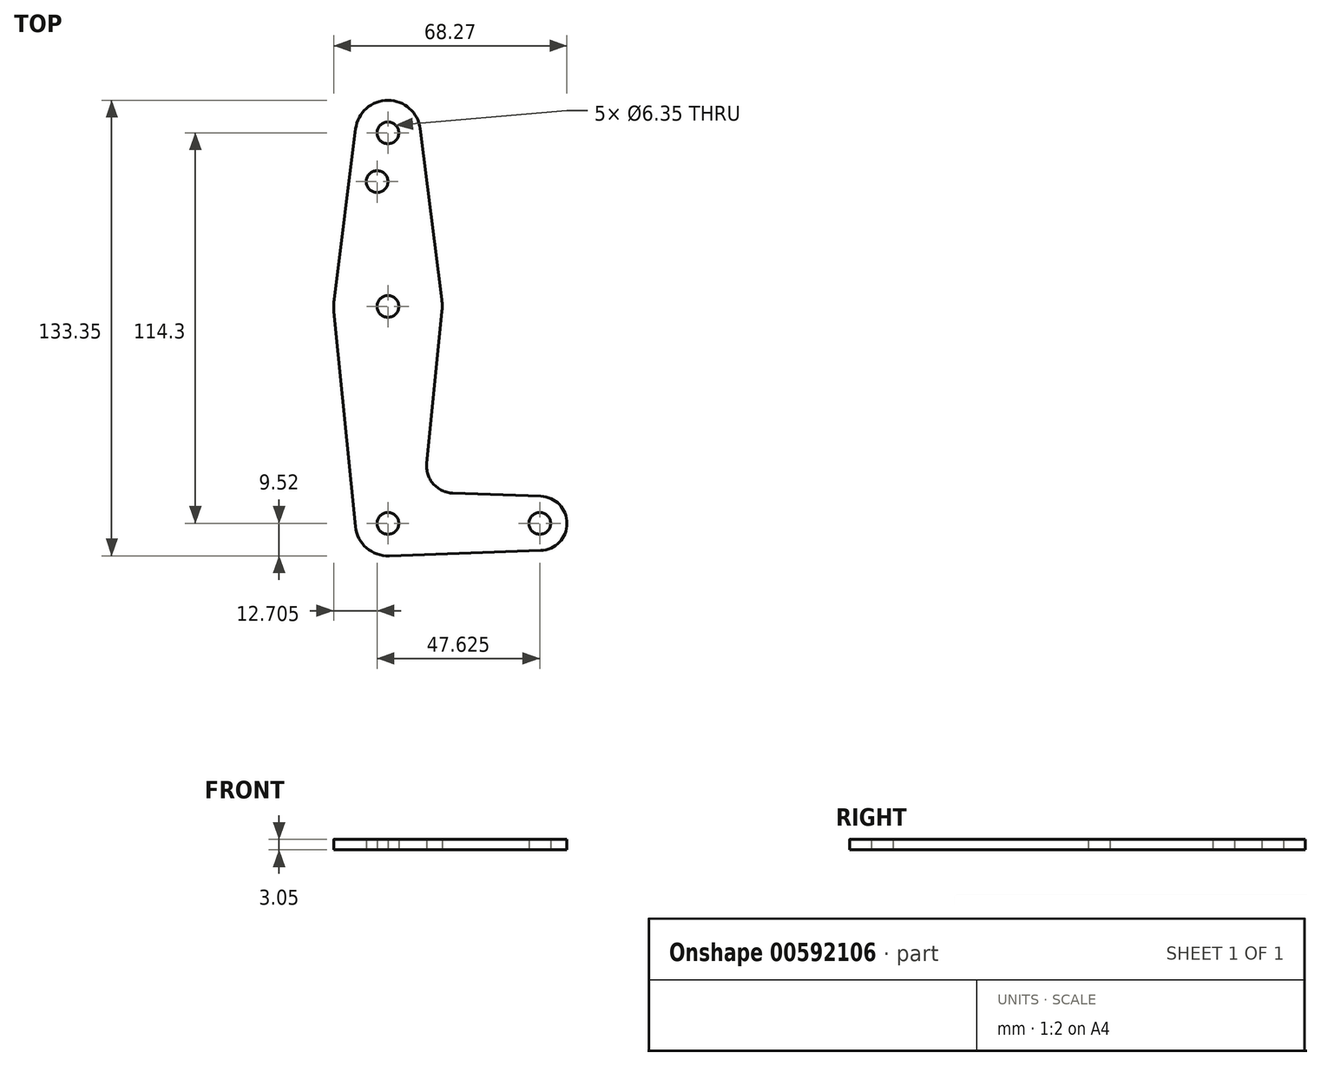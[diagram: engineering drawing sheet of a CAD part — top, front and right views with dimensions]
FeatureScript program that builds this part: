
annotation { "Feature Type Name" : "Feature", "Feature Type Description" : "" }
export const myFeature = defineFeature(function(context is Context, id is Id, definition is map)
    precondition{}
    {
        {
            var Q0;
            Q0=qCreatedBy(makeId("Top.planeOp"),FACE);
            var sketch = newSketch(context, id + "F0", { "sketchPlane" : qUnion([Q0])});
            skLineSegment(sketch, "E0", {"start": v(0, 0) * mm, "end": v(44.45, 0) * mm, "construction": true});
            skLineSegment(sketch, "E1", {"start": v(0, 0) * mm, "end": v(0, 114.3) * mm, "construction": true});
            skCircle(sketch, "E2", {"center": v(0, 0) * mm, "radius": 9.53 * mm});
            skCircle(sketch, "E3", {"center": v(44.45, 0) * mm, "radius": 7.94 * mm});
            skCircle(sketch, "E4", {"center": v(0, 114.3) * mm, "radius": 9.53 * mm});
            skCircle(sketch, "E5", {"center": v(0, 63.5) * mm, "radius": 15.88 * mm});
            skLineSegment(sketch, "E6", {"start": v(-9.45, 115.5) * mm, "end": v(-15.75, 65.48) * mm});
            skLineSegment(sketch, "E7", {"start": v(-15.8, 61.91) * mm, "end": v(-9.48, -0.95) * mm});
            skLineSegment(sketch, "E8", {"start": v(15.8, 61.91) * mm, "end": v(11.34, 17.6) * mm});
            skLineSegment(sketch, "E9", {"start": v(9.45, 115.5) * mm, "end": v(15.75, 65.48) * mm});
            skLineSegment(sketch, "E10", {"start": v(18.97, 8.85) * mm, "end": v(44.73, 7.93) * mm});
            skLineSegment(sketch, "E11", {"start": v(0.34, -9.52) * mm, "end": v(44.73, -7.93) * mm});
            skCircle(sketch, "E12", {"center": v(0, 114.3) * mm, "radius": 3.18 * mm});
            skCircle(sketch, "E13", {"center": v(0, 63.5) * mm, "radius": 3.18 * mm});
            skCircle(sketch, "E14", {"center": v(0, 0) * mm, "radius": 3.18 * mm});
            skCircle(sketch, "E15", {"center": v(44.45, 0) * mm, "radius": 3.18 * mm});
            skCircle(sketch, "E16", {"center": v(-3.18, 100.03) * mm, "radius": 3.18 * mm});
            skArc(sketch, "E17.filletArc", {"start": v(11.34, 17.6) * mm, "mid": v(13.26, 11.57) * mm, "end": v(18.97, 8.85) * mm});
            skSolve(sketch);
        }
        {
            var Q0;
            Q0 = qSketchRegion(id + "F0", true);
            extrude(context, id + "F1", {"entities" : qUnion([Q0]), "depth" : 3.05 * mm, "offsetDistance" : 25.4 * mm});
        }
    });
